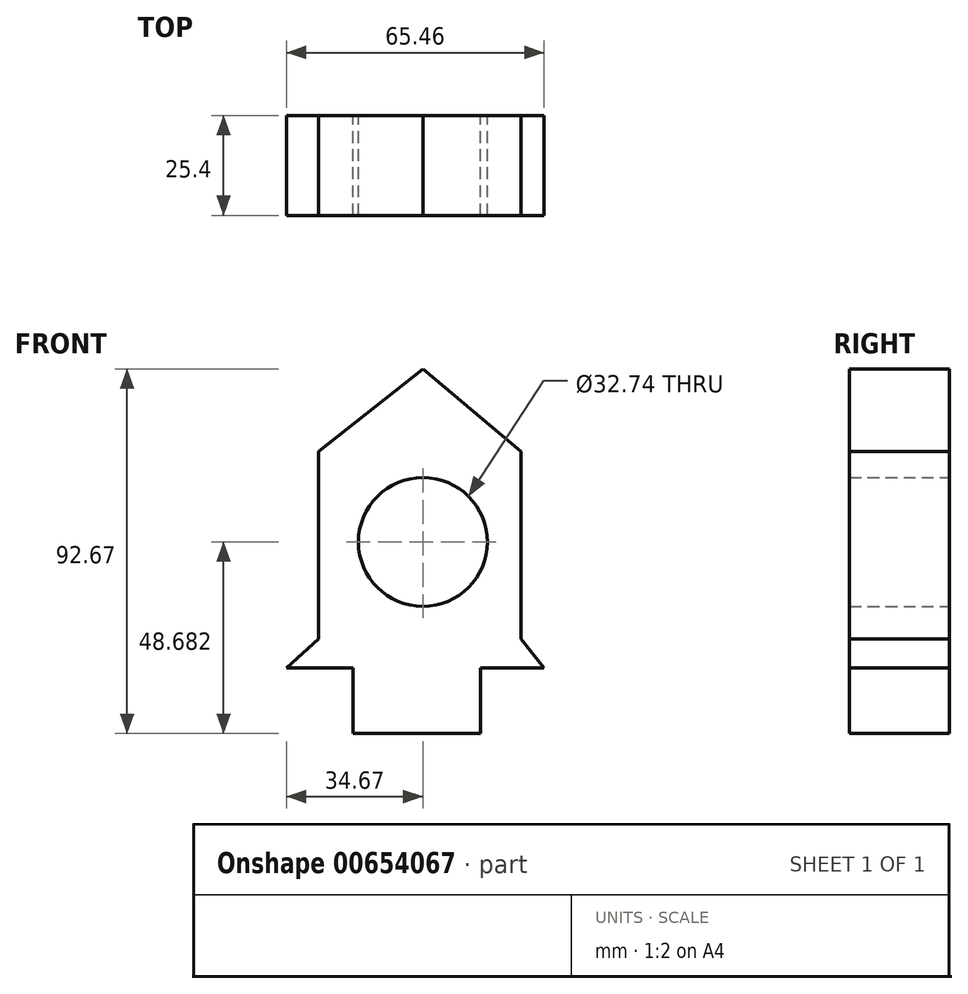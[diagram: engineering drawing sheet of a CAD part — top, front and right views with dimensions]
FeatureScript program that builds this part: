
annotation { "Feature Type Name" : "Feature", "Feature Type Description" : "" }
export const myFeature = defineFeature(function(context is Context, id is Id, definition is map)
    precondition{}
    {
        {
            var Q0;
            Q0=qCreatedBy(makeId("Front.planeOp"),FACE);
            var sketch = newSketch(context, id + "F0", { "sketchPlane" : qUnion([Q0])});
            skLineSegment(sketch, "E0", {"start": v(0, 0) * mm, "end": v(-34.67, 0) * mm});
            skLineSegment(sketch, "E1", {"start": v(-34.67, 0) * mm, "end": v(-26.56, 7.41) * mm});
            skLineSegment(sketch, "E2", {"start": v(-26.56, 7.41) * mm, "end": v(0, 7.41) * mm});
            skLineSegment(sketch, "E3", {"start": v(0, 7.41) * mm, "end": v(0, 0) * mm});
            skLineSegment(sketch, "E4", {"start": v(0, 0) * mm, "end": v(30.79, 0) * mm});
            skLineSegment(sketch, "E5", {"start": v(30.79, 0) * mm, "end": v(24.91, 7.41) * mm});
            skLineSegment(sketch, "E6", {"start": v(24.91, 7.41) * mm, "end": v(0, 7.41) * mm});
            skLineSegment(sketch, "E7", {"start": v(-26.56, 7.41) * mm, "end": v(-26.56, 54.97) * mm});
            skLineSegment(sketch, "E8", {"start": v(-26.56, 54.97) * mm, "end": v(24.91, 54.97) * mm});
            skLineSegment(sketch, "E9", {"start": v(24.91, 54.97) * mm, "end": v(24.91, 7.41) * mm});
            skLineSegment(sketch, "E10", {"start": v(-26.56, 54.97) * mm, "end": v(0, 76.02) * mm});
            skLineSegment(sketch, "E11", {"start": v(0, 76.02) * mm, "end": v(24.91, 54.97) * mm});
            skCircle(sketch, "E12", {"center": v(0, 32.03) * mm, "radius": 16.37 * mm});
            skCircle(sketch, "E13", {"center": v(0, 32.03) * mm, "radius": 13.55 * mm});
            skSolve(sketch);
        }
        {
            var Q0;
            Q0 = qSketchRegion(id + "F0", true);
            extrude(context, id + "F1", {"entities" : qUnion([Q0]), "depth" : 25.4 * mm, "offsetDistance" : 25.4 * mm});
        }
        {
            var Q0;
            Q0=qCreatedBy(makeId("Front.planeOp"),FACE);
            var sketch = newSketch(context, id + "F2", { "sketchPlane" : qUnion([Q0])});
            skLineSegment(sketch, "E14", {"start": v(-34.55, 0) * mm, "end": v(-34.55, -16.65) * mm});
            skLineSegment(sketch, "E15", {"start": v(-34.55, -16.65) * mm, "end": v(29.51, -16.65) * mm});
            skLineSegment(sketch, "E16", {"start": v(29.51, -16.65) * mm, "end": v(29.51, 0) * mm});
            skLineSegment(sketch, "E17", {"start": v(29.51, 0) * mm, "end": v(29.51, -16.65) * mm});
            skLineSegment(sketch, "E18", {"start": v(0, 0) * mm, "end": v(0, -16.65) * mm});
            skLineSegment(sketch, "E19", {"start": v(0, -16.65) * mm, "end": v(14.69, -16.65) * mm});
            skLineSegment(sketch, "E20", {"start": v(14.69, -16.65) * mm, "end": v(14.69, 0) * mm});
            skLineSegment(sketch, "E21", {"start": v(14.69, 0) * mm, "end": v(-17.76, 0) * mm});
            skLineSegment(sketch, "E22", {"start": v(-17.76, 0) * mm, "end": v(-17.76, -16.65) * mm});
            skLineSegment(sketch, "E23", {"start": v(-17.76, -16.65) * mm, "end": v(-34.55, -16.65) * mm});
            skLineSegment(sketch, "E24", {"start": v(-34.55, 0) * mm, "end": v(-17.76, 0) * mm});
            skLineSegment(sketch, "E25", {"start": v(14.69, 0) * mm, "end": v(29.51, 0) * mm});
            skLineSegment(sketch, "E26", {"start": v(-34.55, -16.65) * mm, "end": v(0, -53.01) * mm});
            skLineSegment(sketch, "E27", {"start": v(0, -53.01) * mm, "end": v(29.51, -16.65) * mm});
            skSolve(sketch);
        }
        {
            var Q0;
            {var subQ2=sQuery(id+"F2.wireOp",EDGE,"E18");Q0=makeQuery(id+"F2.imprint","IMPRINT",FACE,{"disambiguationData":[TD([[makeQuery(id+"F2.imprint","IMPRINT",EDGE,{"derivedFrom":subQ2}),-1.0]])]});}
            var Q1;
            {var subQ0=sQuery(id+"F2.wireOp",EDGE,"E18");Q1=makeQuery(id+"F2.imprint","IMPRINT",FACE,{"disambiguationData":[TD([[makeQuery(id+"F2.imprint","IMPRINT",EDGE,{"derivedFrom":subQ0}),1.0]])]});}
            var Q2;
            {var subQ1=sQuery(id+"F2.wireOp",EDGE,"E19");Q2=makeQuery(id+"F2.imprint","IMPRINT",FACE,{"disambiguationData":[TD([[makeQuery(id+"F2.imprint","IMPRINT",EDGE,{"derivedFrom":subQ1}),-1.0]])]});}
            extrude(context, id + "F3", {"entities" : qUnion([Q0, Q1, Q2]), "operationType" : NewBodyOperationType.ADD, "depth" : 25.4 * mm, "offsetDistance" : 25.4 * mm});
        }
    });
